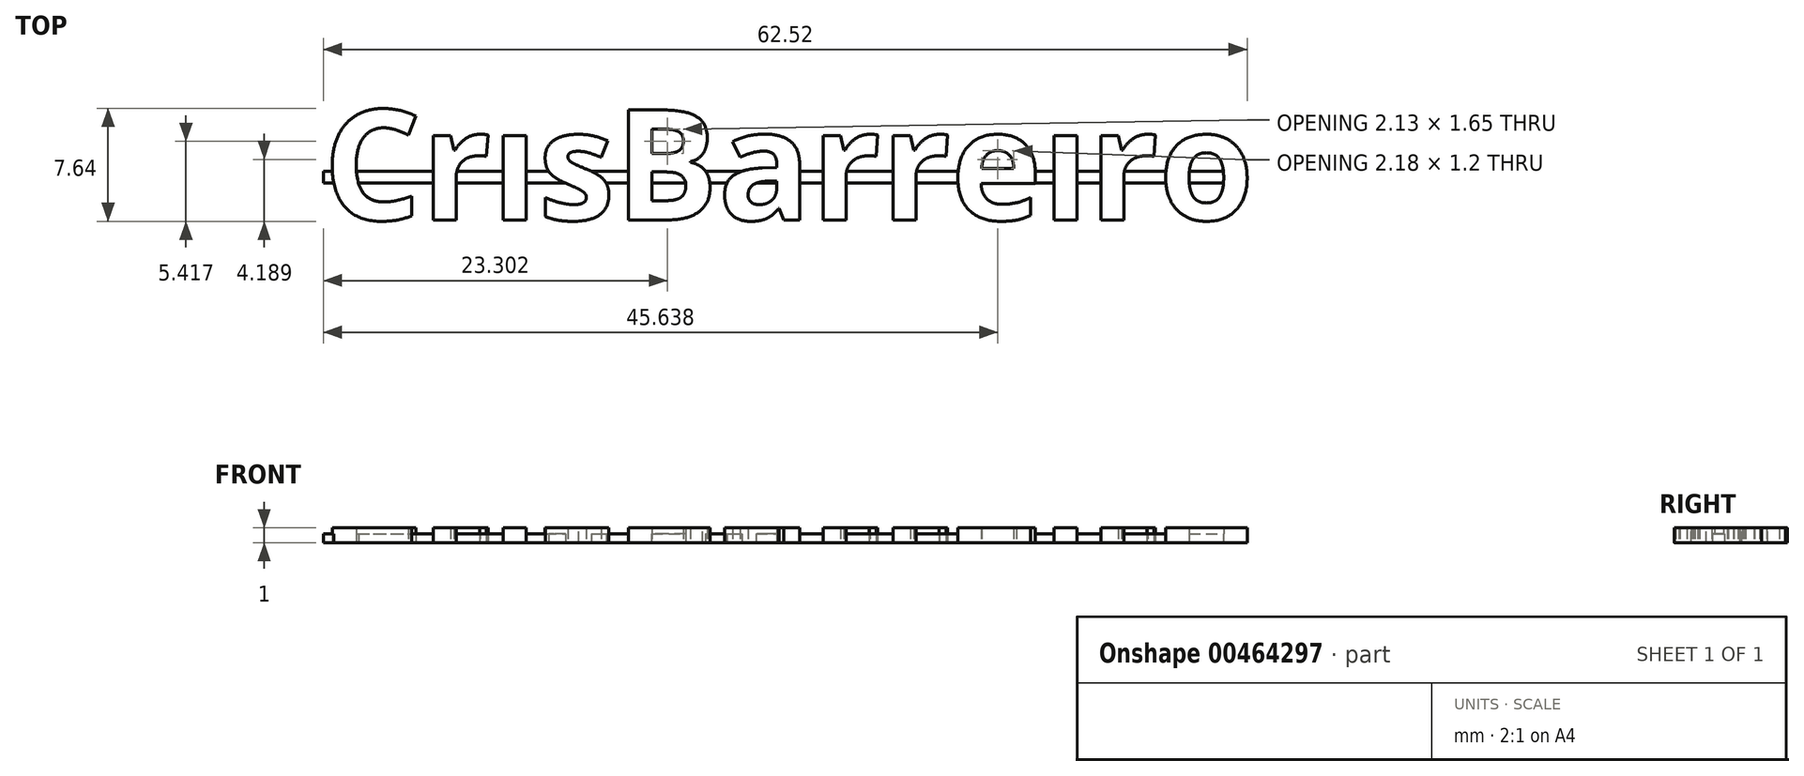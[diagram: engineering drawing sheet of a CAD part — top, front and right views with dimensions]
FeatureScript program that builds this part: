
annotation { "Feature Type Name" : "Feature", "Feature Type Description" : "" }
export const myFeature = defineFeature(function(context is Context, id is Id, definition is map)
    precondition{}
    {
        {
            var Q0;
            Q0=qCreatedBy(makeId("Top.planeOp"),FACE);
            var sketch = newSketch(context, id + "F0", { "sketchPlane" : qUnion([Q0])});
            skText(sketch, "E0", { "text": "CrisBarreiro", "fontName": "OpenSans-Bold.ttf"});
            const initialGuessF0  = {"E0": [0, -0.0075, 1, 0, 0.0075]};
            skSetInitialGuess(sketch, initialGuessF0);
            skSolve(sketch);
        }
        {
            var Q0;
            Q0=qSketchRegion(id+"F0",true);
            extrude(context, id + "F1", {"entities" : qUnion([Q0]), "depth" : 1 * mm});
        }
        {
            var Q0;
            Q0=qCreatedBy(makeId("Top.planeOp"),FACE);
            var sketch = newSketch(context, id + "F2", { "sketchPlane" : qUnion([Q0])});
            skLineSegment(sketch, "E1.bottom", {"start": v(0, -4.2) * mm, "end": v(61.96, -4.2) * mm});
            skLineSegment(sketch, "E1.top", {"start": v(0, -5.02) * mm, "end": v(61.96, -5.02) * mm});
            skLineSegment(sketch, "E1.left", {"start": v(0, -4.2) * mm, "end": v(0, -5.02) * mm});
            skLineSegment(sketch, "E1.right", {"start": v(61.96, -4.2) * mm, "end": v(61.96, -5.02) * mm});
            skSolve(sketch);
        }
        {
            var Q0;
            Q0=qSketchRegion(id+"F2",true);
            extrude(context, id + "F3", {"entities" : qUnion([Q0]), "operationType" : NewBodyOperationType.ADD, "depth" : 0.6 * mm});
        }
        {
            var Q0;
            Q0=makeQuery(id+"F1.opExtrude","SWEPT_BODY",BODY,{"disambiguationData":[OSD([sQuery(id+"F0.wireOp",EDGE,"E0.sketch_text.stroke-159"),sQuery(id+"F0.wireOp",EDGE,"E0.sketch_text.stroke-160"),sQuery(id+"F0.wireOp",EDGE,"E0.sketch_text.stroke-161"),sQuery(id+"F0.wireOp",EDGE,"E0.sketch_text.stroke-162"),sQuery(id+"F0.wireOp",EDGE,"E0.sketch_text.stroke-163")])]});
            var Q1;
            Q1=makeQuery(id+"F1.opExtrude","SWEPT_BODY",BODY,{"disambiguationData":[OSD([sQuery(id+"F0.wireOp",EDGE,"E0.sketch_text.stroke-28"),sQuery(id+"F0.wireOp",EDGE,"E0.sketch_text.stroke-29"),sQuery(id+"F0.wireOp",EDGE,"E0.sketch_text.stroke-30"),sQuery(id+"F0.wireOp",EDGE,"E0.sketch_text.stroke-31"),sQuery(id+"F0.wireOp",EDGE,"E0.sketch_text.stroke-32")])]});
            deleteBodies(context, id + "F4", {"entities" : qUnion([Q0, Q1])});
        }
    });
